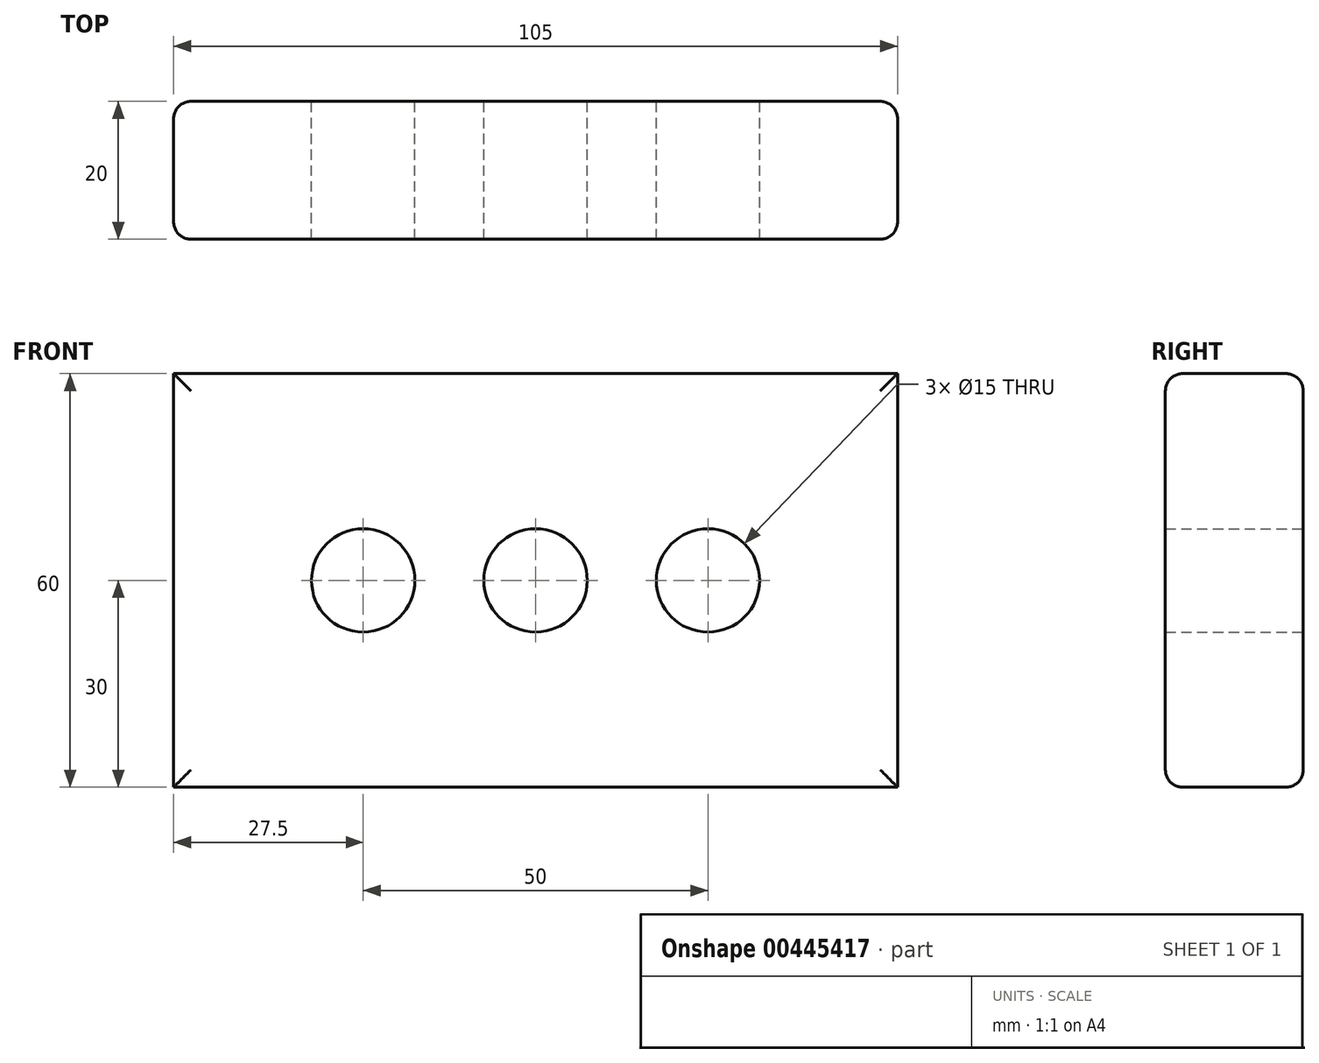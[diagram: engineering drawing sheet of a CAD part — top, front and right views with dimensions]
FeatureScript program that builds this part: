
annotation { "Feature Type Name" : "Feature", "Feature Type Description" : "" }
export const myFeature = defineFeature(function(context is Context, id is Id, definition is map)
    precondition{}
    {
        {
            var Q0;
            Q0=qCreatedBy(makeId("Front.planeOp"),FACE);
            var sketch = newSketch(context, id + "F0", { "sketchPlane" : qUnion([Q0])});
            skLineSegment(sketch, "E0.bottom", {"start": v(52.5, -30) * mm, "end": v(-52.5, -30) * mm});
            skLineSegment(sketch, "E0.top", {"start": v(52.5, 30) * mm, "end": v(-52.5, 30) * mm});
            skLineSegment(sketch, "E0.left", {"start": v(52.5, -30) * mm, "end": v(52.5, 30) * mm});
            skLineSegment(sketch, "E0.right", {"start": v(-52.5, -30) * mm, "end": v(-52.5, 30) * mm});
            skPoint(sketch, "E0.middle", {"position": v(0, 0) * mm});
            skCircle(sketch, "E1", {"center": v(0, 0) * mm, "radius": 7.5 * mm});
            skCircle(sketch, "E2", {"center": v(-25, 0) * mm, "radius": 7.5 * mm});
            skCircle(sketch, "E3", {"center": v(25, 0) * mm, "radius": 7.5 * mm});
            skSolve(sketch);
        }
        {
            var Q0;
            Q0=makeQuery(id+"F0.imprint","IMPRINT",FACE,{"disambiguationData":[TD([[makeQuery(id+"F0.imprint","IMPRINT",EDGE,{"derivedFrom":sQuery(id+"F0.wireOp",EDGE,"E0.bottom")}),-1.0]])]});
            extrude(context, id + "F1", {"entities" : qUnion([Q0]), "depth" : 20 * mm});
        }
        {
            var Q0;
            Q0=makeQuery(id+"F1.opExtrude","CAP_EDGE",EDGE,{"disambiguationData":[OSD([sQuery(id+"F0.wireOp",EDGE,"E0.bottom")])],"isStart":false});
            var Q1;
            Q1=makeQuery(id+"F1.opExtrude","CAP_EDGE",EDGE,{"disambiguationData":[OSD([sQuery(id+"F0.wireOp",EDGE,"E0.right")])],"isStart":false});
            var Q2;
            Q2=makeQuery(id+"F1.opExtrude","CAP_EDGE",EDGE,{"disambiguationData":[OSD([sQuery(id+"F0.wireOp",EDGE,"E0.top")])],"isStart":false});
            var Q3;
            Q3=makeQuery(id+"F1.opExtrude","CAP_EDGE",EDGE,{"disambiguationData":[OSD([sQuery(id+"F0.wireOp",EDGE,"E0.left")])],"isStart":true});
            var Q4;
            Q4=makeQuery(id+"F1.opExtrude","CAP_EDGE",EDGE,{"disambiguationData":[OSD([sQuery(id+"F0.wireOp",EDGE,"E0.bottom")])],"isStart":true});
            var Q5;
            Q5=makeQuery(id+"F1.opExtrude","CAP_EDGE",EDGE,{"disambiguationData":[OSD([sQuery(id+"F0.wireOp",EDGE,"E0.right")])],"isStart":true});
            var Q6;
            Q6=makeQuery(id+"F1.opExtrude","CAP_EDGE",EDGE,{"disambiguationData":[OSD([sQuery(id+"F0.wireOp",EDGE,"E0.top")])],"isStart":true});
            var Q7;
            Q7=makeQuery(id+"F1.opExtrude","CAP_EDGE",EDGE,{"disambiguationData":[OSD([sQuery(id+"F0.wireOp",EDGE,"E0.left")])],"isStart":false});
            fillet(context, id + "F2", {"entities" : qUnion([Q0, Q1, Q2, Q3, Q4, Q5, Q6, Q7]), "radius" : 2.5 * mm, "tangentPropagation" : true, "allowEdgeOverflow" : false});
        }
    });
